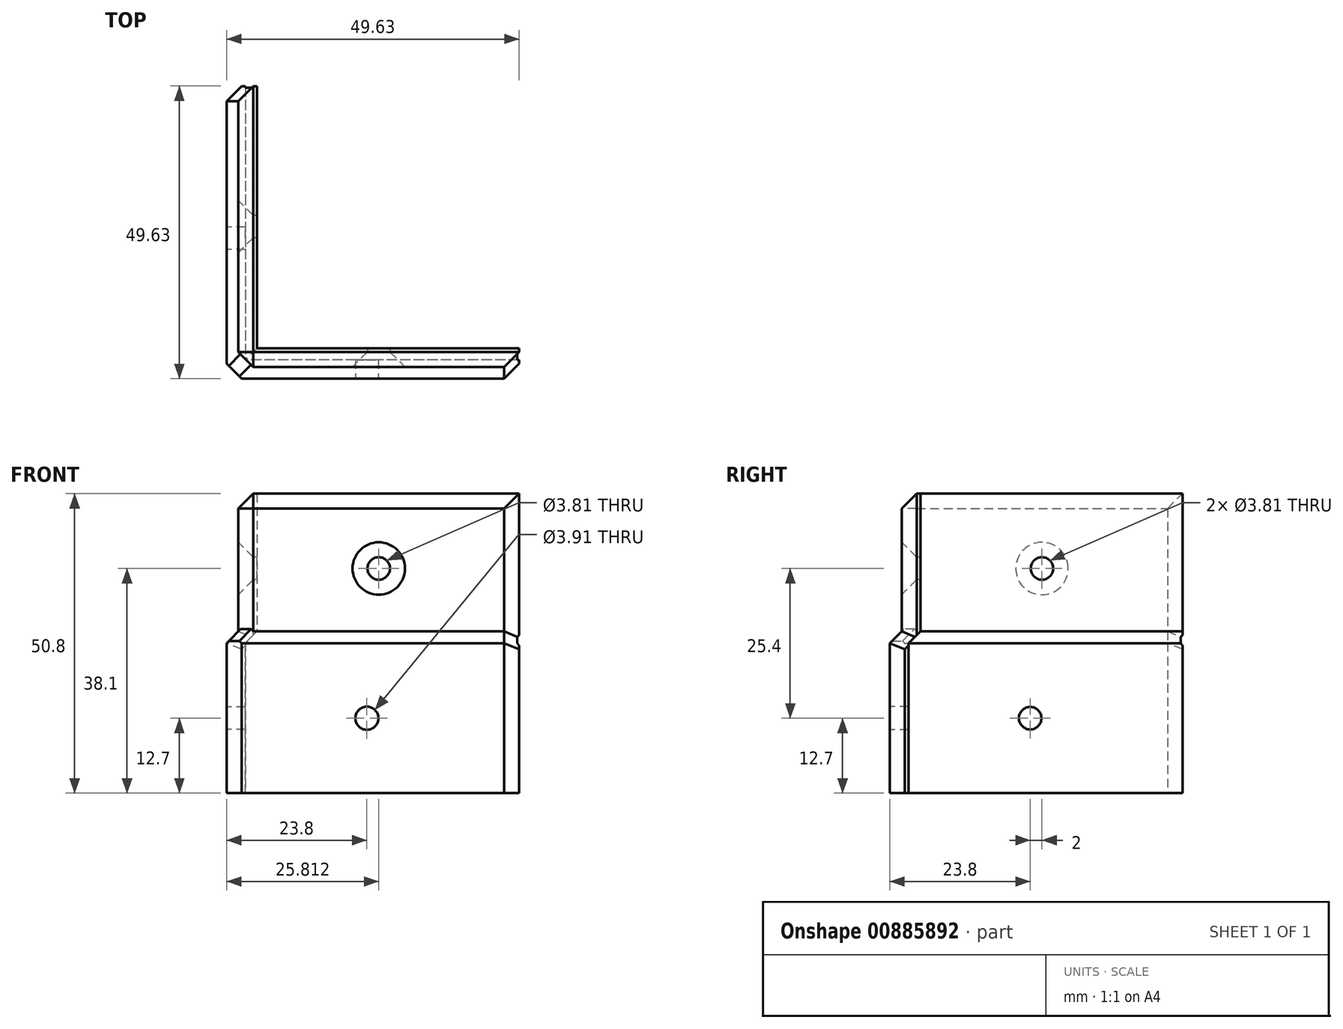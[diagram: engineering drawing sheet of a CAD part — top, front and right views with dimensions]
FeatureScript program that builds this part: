
annotation { "Feature Type Name" : "Feature", "Feature Type Description" : "" }
export const myFeature = defineFeature(function(context is Context, id is Id, definition is map)
    precondition{}
    {
        {
            var Q0;
            Q0=qCreatedBy(makeId("Top.planeOp"),FACE);
            var sketch = newSketch(context, id + "F0", { "sketchPlane" : qUnion([Q0])});
            skLineSegment(sketch, "E0.bottom", {"start": v(0, 0) * mm, "end": v(47.62, 0) * mm});
            skLineSegment(sketch, "E0.top", {"start": v(0, 47.63) * mm, "end": v(3.17, 47.63) * mm});
            skLineSegment(sketch, "E0.left", {"start": v(0, 0) * mm, "end": v(0, 47.63) * mm});
            skLineSegment(sketch, "E0.right", {"start": v(47.63, 0) * mm, "end": v(47.63, 3.18) * mm});
            skLineSegment(sketch, "E1.top", {"start": v(47.63, 3.18) * mm, "end": v(3.17, 3.17) * mm});
            skLineSegment(sketch, "E1.right", {"start": v(3.17, 47.63) * mm, "end": v(3.17, 3.18) * mm});
            skSolve(sketch);
        }
        {
            var Q0;
            Q0 = qSketchRegion(id + "F0", true);
            extrude(context, id + "F1", {"entities" : qUnion([Q0]), "depth" : 25.4 * mm, "offsetDistance" : 25.4 * mm});
        }
        {
            var Q0;
            Q0=makeQuery(id+"F1.opExtrude","CAP_FACE",FACE,{"disambiguationData":[OSD([sQuery(id+"F0.wireOp",EDGE,"E0.bottom"),sQuery(id+"F0.wireOp",EDGE,"E0.top"),sQuery(id+"F0.wireOp",EDGE,"E0.left"),sQuery(id+"F0.wireOp",EDGE,"E0.right"),sQuery(id+"F0.wireOp",EDGE,"E1.top"),sQuery(id+"F0.wireOp",EDGE,"E1.right")])],"isStart":false});
            var sketch = newSketch(context, id + "F2", { "sketchPlane" : qUnion([Q0])});
            skLineSegment(sketch, "E2.bottom", {"start": v(5.17, 49.62) * mm, "end": v(2, 49.62) * mm});
            skLineSegment(sketch, "E2.top", {"start": v(49.63, 2) * mm, "end": v(2, 2) * mm});
            skLineSegment(sketch, "E2.left", {"start": v(49.63, 5.17) * mm, "end": v(49.63, 2) * mm});
            skLineSegment(sketch, "E2.right", {"start": v(2, 49.63) * mm, "end": v(2, 2) * mm});
            skLineSegment(sketch, "E3.top", {"start": v(49.63, 5.17) * mm, "end": v(5.17, 5.17) * mm});
            skLineSegment(sketch, "E3.right", {"start": v(5.17, 49.63) * mm, "end": v(5.17, 5.17) * mm});
            skSolve(sketch);
        }
        {
            var Q0;
            Q0 = qSketchRegion(id + "F2", true);
            extrude(context, id + "F3", {"entities" : qUnion([Q0]), "operationType" : NewBodyOperationType.ADD, "depth" : 25.4 * mm, "offsetDistance" : 25.4 * mm});
        }
        {
            var Q0;
            Q0=makeQuery(id+"F1.opExtrude","SWEPT_FACE",FACE,{"disambiguationData":[OSD([sQuery(id+"F0.wireOp",EDGE,"E0.bottom")])]});
            var sketch = newSketch(context, id + "F4", { "sketchPlane" : qUnion([Q0])});
            skCircle(sketch, "E4", {"center": v(23.8, 12.7) * mm, "radius": 1.96 * mm});
            skCircle(sketch, "E5", {"center": v(25.81, 38.1) * mm, "radius": 1.9 * mm});
            skSolve(sketch);
        }
        {
            var Q0;
            Q0 = qSketchRegion(id + "F4", true);
            extrude(context, id + "F5", {"entities" : qUnion([Q0]), "operationType" : NewBodyOperationType.REMOVE, "oppositeDirection" : true, "depth" : 25.4 * mm, "offsetDistance" : 25.4 * mm});
        }
        {
            var Q0;
            Q0=makeQuery(id+"F1.opExtrude","SWEPT_FACE",FACE,{"disambiguationData":[OSD([sQuery(id+"F0.wireOp",EDGE,"E0.left")])]});
            var sketch = newSketch(context, id + "F6", { "sketchPlane" : qUnion([Q0])});
            skCircle(sketch, "E6", {"center": v(-23.8, 12.7) * mm, "radius": 1.9 * mm});
            skCircle(sketch, "E7", {"center": v(-25.8, 38.1) * mm, "radius": 1.9 * mm});
            skSolve(sketch);
        }
        {
            var Q0;
            Q0 = qSketchRegion(id + "F6", true);
            extrude(context, id + "F7", {"entities" : qUnion([Q0]), "operationType" : NewBodyOperationType.REMOVE, "oppositeDirection" : true, "depth" : 25.4 * mm, "offsetDistance" : 25.4 * mm});
        }
        {
            var Q0;
            Q0=makeQuery(id+"F7.boolean.opBoolean","COPY",EDGE,{"derivedFrom":makeQuery(id+"F7.opExtrude","CAP_EDGE",EDGE,{"disambiguationData":[OSD([sQuery(id+"F6.wireOp",EDGE,"E6")])],"isStart":true})});
            var Q1;
            Q1=makeQuery(id+"F7.boolean.opBoolean","INTERSECT",EDGE,{"derivedFrom":[makeQuery(id+"F3.opExtrude","SWEPT_FACE",FACE,{"disambiguationData":[OSD([sQuery(id+"F2.wireOp",EDGE,"E2.right")])]}),makeQuery(id+"F7.opExtrude","SWEPT_FACE",FACE,{"disambiguationData":[OSD([sQuery(id+"F6.wireOp",EDGE,"E7")])]})]});
            var Q2;
            Q2=makeQuery(id+"F5.boolean.opBoolean","INTERSECT",EDGE,{"derivedFrom":[makeQuery(id+"F3.opExtrude","SWEPT_FACE",FACE,{"disambiguationData":[OSD([sQuery(id+"F2.wireOp",EDGE,"E2.top")])]}),makeQuery(id+"F5.opExtrude","SWEPT_FACE",FACE,{"disambiguationData":[OSD([sQuery(id+"F4.wireOp",EDGE,"E5")])]})]});
            var Q3;
            Q3=makeQuery(id+"F5.boolean.opBoolean","COPY",EDGE,{"derivedFrom":makeQuery(id+"F5.opExtrude","CAP_EDGE",EDGE,{"disambiguationData":[OSD([sQuery(id+"F4.wireOp",EDGE,"E4")])],"isStart":true})});
            chamfer(context, id + "F8", {"entities" : qUnion([Q0, Q1, Q2, Q3]), "width" : 2.54 * mm, "tangentPropagation" : true});
        }
        {
            var Q0;
            Q0=makeQuery(id+"F1.opExtrude","SWEPT_FACE",FACE,{"disambiguationData":[OSD([sQuery(id+"F0.wireOp",EDGE,"E0.top")])]});
            var Q1;
            Q1=makeQuery(id+"F3.opExtrude","SWEPT_FACE",FACE,{"disambiguationData":[OSD([sQuery(id+"F2.wireOp",EDGE,"E2.bottom")])]});
            extrude(context, id + "F9", {"entities" : qUnion([Q0]), "operationType" : NewBodyOperationType.ADD, "endBound" : BoundingType.UP_TO_SURFACE, "depth" : 25.4 * mm, "endBoundEntityFace" : qUnion([Q1]), "offsetDistance" : 25.4 * mm});
        }
        {
            var Q0;
            Q0=makeQuery(id+"F1.opExtrude","SWEPT_FACE",FACE,{"disambiguationData":[OSD([sQuery(id+"F0.wireOp",EDGE,"E0.right")])]});
            var Q1;
            Q1=makeQuery(id+"F3.opExtrude","SWEPT_FACE",FACE,{"disambiguationData":[OSD([sQuery(id+"F2.wireOp",EDGE,"E2.left")])]});
            extrude(context, id + "F10", {"entities" : qUnion([Q0]), "operationType" : NewBodyOperationType.ADD, "endBound" : BoundingType.UP_TO_SURFACE, "depth" : 25.4 * mm, "endBoundEntityFace" : qUnion([Q1]), "offsetDistance" : 25.4 * mm});
        }
        {
            var Q0;
            {var subQ0=sQuery(id+"F2.wireOp",EDGE,"E2.top");var subQ2=makeQuery(id+"F3.opExtrude","CAP_EDGE",EDGE,{"disambiguationData":[OSD([subQ0])],"isStart":true});Q0=makeQuery(id+"F10.boolean.opBoolean","MERGE",EDGE,{"derivedFrom":[makeQuery(id+"F3.boolean.opBoolean","SPLIT",EDGE,{"disambiguationData":[topologyDisambiguationEdgeConnected([makeQuery(id+"F3.opExtrude","CAP_FACE",FACE,{"disambiguationData":[OSD([sQuery(id+"F2.wireOp",EDGE,"E2.bottom"),subQ0,sQuery(id+"F2.wireOp",EDGE,"E2.left"),sQuery(id+"F2.wireOp",EDGE,"E2.right"),sQuery(id+"F2.wireOp",EDGE,"E3.top"),sQuery(id+"F2.wireOp",EDGE,"E3.right")])],"isStart":true})])],"derivedFrom":subQ2}),makeQuery(id+"F3.boolean.opBoolean","SPLIT",EDGE,{"disambiguationData":[topologyDisambiguationEdgeConnected([makeQuery(id+"F1.opExtrude","CAP_FACE",FACE,{"disambiguationData":[OSD([sQuery(id+"F0.wireOp",EDGE,"E0.bottom"),sQuery(id+"F0.wireOp",EDGE,"E0.top"),sQuery(id+"F0.wireOp",EDGE,"E0.left"),sQuery(id+"F0.wireOp",EDGE,"E0.right"),sQuery(id+"F0.wireOp",EDGE,"E1.top"),sQuery(id+"F0.wireOp",EDGE,"E1.right")])],"isStart":false})])],"derivedFrom":subQ2})]});}
            var Q1;
            {var subQ0=sQuery(id+"F2.wireOp",EDGE,"E2.right");var subQ2=makeQuery(id+"F3.opExtrude","CAP_EDGE",EDGE,{"disambiguationData":[OSD([subQ0])],"isStart":true});Q1=makeQuery(id+"F9.boolean.opBoolean","MERGE",EDGE,{"derivedFrom":[makeQuery(id+"F3.boolean.opBoolean","SPLIT",EDGE,{"disambiguationData":[topologyDisambiguationEdgeConnected([makeQuery(id+"F3.opExtrude","CAP_FACE",FACE,{"disambiguationData":[OSD([sQuery(id+"F2.wireOp",EDGE,"E2.bottom"),sQuery(id+"F2.wireOp",EDGE,"E2.top"),sQuery(id+"F2.wireOp",EDGE,"E2.left"),subQ0,sQuery(id+"F2.wireOp",EDGE,"E3.top"),sQuery(id+"F2.wireOp",EDGE,"E3.right")])],"isStart":true})])],"derivedFrom":subQ2}),makeQuery(id+"F3.boolean.opBoolean","SPLIT",EDGE,{"disambiguationData":[topologyDisambiguationEdgeConnected([makeQuery(id+"F1.opExtrude","CAP_FACE",FACE,{"disambiguationData":[OSD([sQuery(id+"F0.wireOp",EDGE,"E0.bottom"),sQuery(id+"F0.wireOp",EDGE,"E0.top"),sQuery(id+"F0.wireOp",EDGE,"E0.left"),sQuery(id+"F0.wireOp",EDGE,"E0.right"),sQuery(id+"F0.wireOp",EDGE,"E1.top"),sQuery(id+"F0.wireOp",EDGE,"E1.right")])],"isStart":false})])],"derivedFrom":subQ2})]});}
            var Q2;
            Q2=makeQuery(id+"F3.opExtrude","CAP_EDGE",EDGE,{"disambiguationData":[OSD([sQuery(id+"F2.wireOp",EDGE,"E3.top")])],"isStart":true});
            var Q3;
            Q3=makeQuery(id+"F3.opExtrude","CAP_EDGE",EDGE,{"disambiguationData":[OSD([sQuery(id+"F2.wireOp",EDGE,"E3.right")])],"isStart":true});
            chamfer(context, id + "F11", {"entities" : qUnion([Q0, Q1, Q2, Q3]), "width" : 2.03 * mm, "tangentPropagation" : true});
        }
        {
            var Q0;
            Q0=makeQuery(id+"F3.opExtrude","SWEPT_EDGE",EDGE,{"disambiguationData":[OSD([sQuery(id+"F2.wireOp",EDGE,"E2.top"),sQuery(id+"F2.wireOp",EDGE,"E2.left")])]});
            var Q1;
            {var subQ0=sQuery(id+"F0.wireOp",EDGE,"E0.right");var subQ1=sQuery(id+"F2.wireOp",EDGE,"E2.left");var subQ2=sQuery(id+"F2.wireOp",EDGE,"E2.top");var subQ4=makeQuery(id+"F3.opExtrude","CAP_EDGE",EDGE,{"disambiguationData":[OSD([subQ2])],"isStart":true});Q1=makeQuery(id+"F11.opChamfer","BLEND_EDGE",EDGE,{"blendedFrom":[makeQuery(id+"F10.boolean.opBoolean","MERGE",EDGE,{"derivedFrom":[makeQuery(id+"F3.boolean.opBoolean","SPLIT",EDGE,{"disambiguationData":[topologyDisambiguationEdgeConnected([makeQuery(id+"F3.opExtrude","CAP_FACE",FACE,{"disambiguationData":[OSD([sQuery(id+"F2.wireOp",EDGE,"E2.bottom"),subQ2,subQ1,sQuery(id+"F2.wireOp",EDGE,"E2.right"),sQuery(id+"F2.wireOp",EDGE,"E3.top"),sQuery(id+"F2.wireOp",EDGE,"E3.right")])],"isStart":true})])],"derivedFrom":subQ4}),makeQuery(id+"F3.boolean.opBoolean","SPLIT",EDGE,{"disambiguationData":[topologyDisambiguationEdgeConnected([makeQuery(id+"F1.opExtrude","CAP_FACE",FACE,{"disambiguationData":[OSD([sQuery(id+"F0.wireOp",EDGE,"E0.bottom"),sQuery(id+"F0.wireOp",EDGE,"E0.top"),sQuery(id+"F0.wireOp",EDGE,"E0.left"),subQ0,sQuery(id+"F0.wireOp",EDGE,"E1.top"),sQuery(id+"F0.wireOp",EDGE,"E1.right")])],"isStart":false})])],"derivedFrom":subQ4})]}),makeQuery(id+"F10.boolean.opBoolean","MERGE",FACE,{"derivedFrom":[makeQuery(id+"F3.opExtrude","SWEPT_FACE",FACE,{"disambiguationData":[OSD([subQ1])]}),makeQuery(id+"F10.opExtrude","CAP_FACE",FACE,{"disambiguationData":[OSD([subQ0])],"isStart":false})]})],"blendedInto":[makeQuery(id+"F10.boolean.opBoolean","MERGE",FACE,{"derivedFrom":[makeQuery(id+"F3.opExtrude","SWEPT_FACE",FACE,{"disambiguationData":[OSD([subQ1])]}),makeQuery(id+"F10.opExtrude","CAP_FACE",FACE,{"disambiguationData":[OSD([subQ0])],"isStart":false})]})]});}
            var Q2;
            Q2=makeQuery(id+"F10.opExtrude","CAP_EDGE",EDGE,{"disambiguationData":[OSD([sQuery(id+"F0.wireOp",EDGE,"E0.bottom"),sQuery(id+"F0.wireOp",EDGE,"E0.right")])],"isStart":false});
            var Q3;
            Q3=makeQuery(id+"F3.opExtrude","SWEPT_EDGE",EDGE,{"disambiguationData":[OSD([sQuery(id+"F2.wireOp",EDGE,"E2.bottom"),sQuery(id+"F2.wireOp",EDGE,"E2.right")])]});
            var Q4;
            {var subQ0=sQuery(id+"F0.wireOp",EDGE,"E0.top");var subQ1=sQuery(id+"F2.wireOp",EDGE,"E2.bottom");var subQ2=sQuery(id+"F2.wireOp",EDGE,"E2.right");var subQ4=makeQuery(id+"F3.opExtrude","CAP_EDGE",EDGE,{"disambiguationData":[OSD([subQ2])],"isStart":true});Q4=makeQuery(id+"F11.opChamfer","BLEND_EDGE",EDGE,{"blendedFrom":[makeQuery(id+"F9.boolean.opBoolean","MERGE",EDGE,{"derivedFrom":[makeQuery(id+"F3.boolean.opBoolean","SPLIT",EDGE,{"disambiguationData":[topologyDisambiguationEdgeConnected([makeQuery(id+"F3.opExtrude","CAP_FACE",FACE,{"disambiguationData":[OSD([subQ1,sQuery(id+"F2.wireOp",EDGE,"E2.top"),sQuery(id+"F2.wireOp",EDGE,"E2.left"),subQ2,sQuery(id+"F2.wireOp",EDGE,"E3.top"),sQuery(id+"F2.wireOp",EDGE,"E3.right")])],"isStart":true})])],"derivedFrom":subQ4}),makeQuery(id+"F3.boolean.opBoolean","SPLIT",EDGE,{"disambiguationData":[topologyDisambiguationEdgeConnected([makeQuery(id+"F1.opExtrude","CAP_FACE",FACE,{"disambiguationData":[OSD([sQuery(id+"F0.wireOp",EDGE,"E0.bottom"),subQ0,sQuery(id+"F0.wireOp",EDGE,"E0.left"),sQuery(id+"F0.wireOp",EDGE,"E0.right"),sQuery(id+"F0.wireOp",EDGE,"E1.top"),sQuery(id+"F0.wireOp",EDGE,"E1.right")])],"isStart":false})])],"derivedFrom":subQ4})]}),makeQuery(id+"F9.boolean.opBoolean","MERGE",FACE,{"derivedFrom":[makeQuery(id+"F3.opExtrude","SWEPT_FACE",FACE,{"disambiguationData":[OSD([subQ1])]}),makeQuery(id+"F9.opExtrude","CAP_FACE",FACE,{"disambiguationData":[OSD([subQ0])],"isStart":false})]})],"blendedInto":[makeQuery(id+"F9.boolean.opBoolean","MERGE",FACE,{"derivedFrom":[makeQuery(id+"F3.opExtrude","SWEPT_FACE",FACE,{"disambiguationData":[OSD([subQ1])]}),makeQuery(id+"F9.opExtrude","CAP_FACE",FACE,{"disambiguationData":[OSD([subQ0])],"isStart":false})]})]});}
            var Q5;
            Q5=makeQuery(id+"F9.opExtrude","CAP_EDGE",EDGE,{"disambiguationData":[OSD([sQuery(id+"F0.wireOp",EDGE,"E0.top"),sQuery(id+"F0.wireOp",EDGE,"E0.left")])],"isStart":false});
            var Q6;
            Q6=makeQuery(id+"F3.opExtrude","CAP_EDGE",EDGE,{"disambiguationData":[OSD([sQuery(id+"F2.wireOp",EDGE,"E2.right")])],"isStart":false});
            var Q7;
            Q7=makeQuery(id+"F3.opExtrude","CAP_EDGE",EDGE,{"disambiguationData":[OSD([sQuery(id+"F2.wireOp",EDGE,"E2.top")])],"isStart":false});
            var Q8;
            Q8=makeQuery(id+"F3.opExtrude","SWEPT_EDGE",EDGE,{"disambiguationData":[OSD([sQuery(id+"F2.wireOp",EDGE,"E2.top"),sQuery(id+"F2.wireOp",EDGE,"E2.right")])]});
            var Q9;
            Q9=makeQuery(id+"F1.opExtrude","SWEPT_EDGE",EDGE,{"disambiguationData":[OSD([sQuery(id+"F0.wireOp",EDGE,"E0.bottom"),sQuery(id+"F0.wireOp",EDGE,"E0.left")])]});
            var Q10;
            {var subQ0=makeQuery(id+"F1.opExtrude","CAP_FACE",FACE,{"disambiguationData":[OSD([sQuery(id+"F0.wireOp",EDGE,"E0.bottom"),sQuery(id+"F0.wireOp",EDGE,"E0.top"),sQuery(id+"F0.wireOp",EDGE,"E0.left"),sQuery(id+"F0.wireOp",EDGE,"E0.right"),sQuery(id+"F0.wireOp",EDGE,"E1.top"),sQuery(id+"F0.wireOp",EDGE,"E1.right")])],"isStart":false});var subQ1=sQuery(id+"F2.wireOp",EDGE,"E2.top");var subQ3=makeQuery(id+"F3.opExtrude","CAP_EDGE",EDGE,{"disambiguationData":[OSD([subQ1])],"isStart":true});var subQ4=sQuery(id+"F2.wireOp",EDGE,"E2.right");var subQ5=makeQuery(id+"F3.opExtrude","CAP_FACE",FACE,{"disambiguationData":[OSD([sQuery(id+"F2.wireOp",EDGE,"E2.bottom"),subQ1,sQuery(id+"F2.wireOp",EDGE,"E2.left"),subQ4,sQuery(id+"F2.wireOp",EDGE,"E3.top"),sQuery(id+"F2.wireOp",EDGE,"E3.right")])],"isStart":true});var subQ7=makeQuery(id+"F3.opExtrude","CAP_EDGE",EDGE,{"disambiguationData":[OSD([subQ4])],"isStart":true});Q10=makeQuery(id+"F11.opChamfer","BLEND_EDGE",EDGE,{"blendedFrom":[makeQuery(id+"F9.boolean.opBoolean","MERGE",EDGE,{"derivedFrom":[makeQuery(id+"F3.boolean.opBoolean","SPLIT",EDGE,{"disambiguationData":[topologyDisambiguationEdgeConnected([subQ5])],"derivedFrom":subQ7}),makeQuery(id+"F3.boolean.opBoolean","SPLIT",EDGE,{"disambiguationData":[topologyDisambiguationEdgeConnected([subQ0])],"derivedFrom":subQ7})]}),makeQuery(id+"F10.boolean.opBoolean","MERGE",EDGE,{"derivedFrom":[makeQuery(id+"F3.boolean.opBoolean","SPLIT",EDGE,{"disambiguationData":[topologyDisambiguationEdgeConnected([subQ5])],"derivedFrom":subQ3}),makeQuery(id+"F3.boolean.opBoolean","SPLIT",EDGE,{"disambiguationData":[topologyDisambiguationEdgeConnected([subQ0])],"derivedFrom":subQ3})]})],"blendedInto":[]});}
            chamfer(context, id + "F12", {"entities" : qUnion([Q0, Q1, Q2, Q3, Q4, Q5, Q6, Q7, Q8, Q9, Q10]), "width" : 2.54 * mm, "tangentPropagation" : true});
        }
    });
